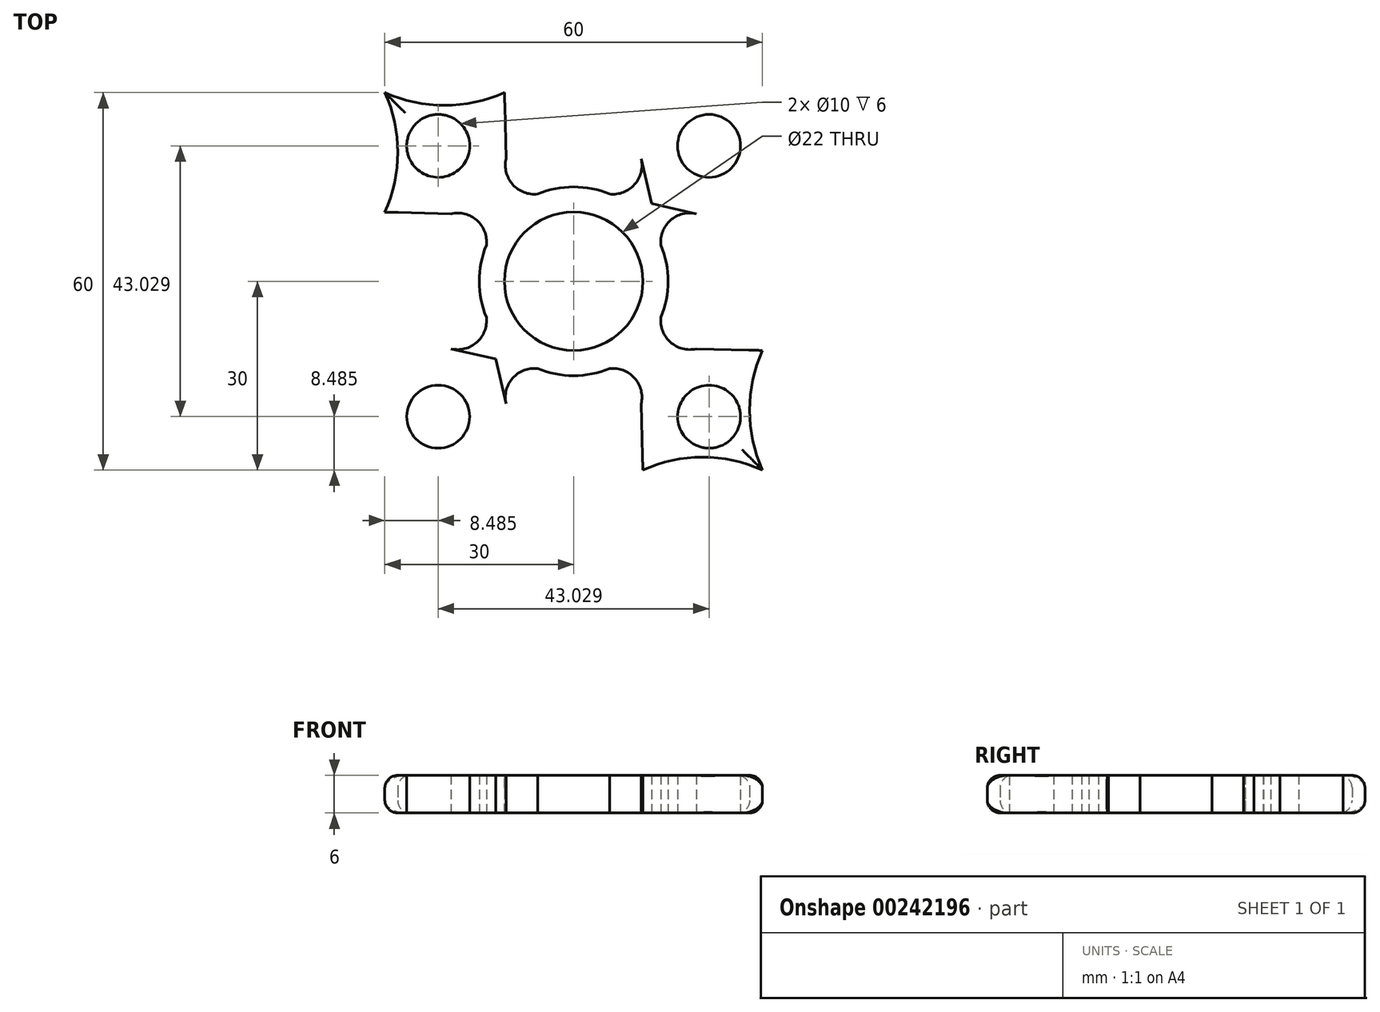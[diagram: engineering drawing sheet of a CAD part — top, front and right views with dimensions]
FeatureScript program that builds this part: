
annotation { "Feature Type Name" : "Feature", "Feature Type Description" : "" }
export const myFeature = defineFeature(function(context is Context, id is Id, definition is map)
    precondition{}
    {
        {
            var Q0;
            Q0=qCreatedBy(makeId("Top.planeOp"),FACE);
            var sketch = newSketch(context, id + "F0", { "sketchPlane" : qUnion([Q0])});
            skLineSegment(sketch, "E0.bottom", {"start": v(30, -30) * mm, "end": v(-30, -30) * mm});
            skLineSegment(sketch, "E0.top", {"start": v(30, 30) * mm, "end": v(-30, 30) * mm});
            skLineSegment(sketch, "E0.left", {"start": v(30, -30) * mm, "end": v(30, 30) * mm});
            skLineSegment(sketch, "E0.right", {"start": v(-30, -30) * mm, "end": v(-30, 30) * mm});
            skPoint(sketch, "E0.middle", {"position": v(0, 0) * mm});
            skCircle(sketch, "E1", {"center": v(0, 0) * mm, "radius": 11 * mm});
            skLineSegment(sketch, "E2", {"start": v(-30, 30) * mm, "end": v(30, -30) * mm, "construction": true});
            skCircle(sketch, "E3", {"center": v(-21.51, 21.51) * mm, "radius": 5 * mm});
            skCircle(sketch, "E4.MirrorC", {"center": v(21.51, 21.51) * mm, "radius": 5 * mm});
            skCircle(sketch, "E5.MirrorC", {"center": v(-21.51, -21.51) * mm, "radius": 5 * mm});
            skCircle(sketch, "E6.MirrorC", {"center": v(21.51, -21.51) * mm, "radius": 5 * mm});
            skCircle(sketch, "E7", {"center": v(0, 0) * mm, "radius": 15 * mm});
            skLineSegment(sketch, "E8", {"start": v(-10.99, 30) * mm, "end": v(-10.53, 10.68) * mm});
            skLineSegment(sketch, "E9.MirrorCS", {"start": v(10.99, 30) * mm, "end": v(10.53, 10.68) * mm});
            skLineSegment(sketch, "E10.MirrorCS", {"start": v(-10.99, -30) * mm, "end": v(-10.53, -10.68) * mm});
            skLineSegment(sketch, "E11.MirrorCS", {"start": v(10.99, -30) * mm, "end": v(10.53, -10.68) * mm});
            skLineSegment(sketch, "E12.MirrorCS", {"start": v(-30, 10.99) * mm, "end": v(-10.68, 10.53) * mm});
            skLineSegment(sketch, "E13.MirrorCS", {"start": v(-30, -10.99) * mm, "end": v(-10.68, -10.53) * mm});
            skLineSegment(sketch, "E14.MirrorCS", {"start": v(30, 10.99) * mm, "end": v(10.68, 10.53) * mm});
            skLineSegment(sketch, "E15.MirrorCS", {"start": v(30, -10.99) * mm, "end": v(10.68, -10.53) * mm});
            skLineSegment(sketch, "E16", {"start": v(30, -30) * mm, "end": v(-49.77, 49.77) * mm, "construction": true});
            skLineSegment(sketch, "E17", {"start": v(-5.73, -13.86) * mm, "end": v(-19.48, -10.74) * mm});
            skLineSegment(sketch, "E18.MirrorCS", {"start": v(5.73, -13.86) * mm, "end": v(19.48, -10.74) * mm});
            skLineSegment(sketch, "E19.MirrorCS", {"start": v(13.86, 5.73) * mm, "end": v(10.74, 19.48) * mm});
            skLineSegment(sketch, "E20.MirrorCS", {"start": v(13.86, -5.73) * mm, "end": v(10.74, -19.48) * mm});
            skLineSegment(sketch, "E21.MirrorCS", {"start": v(-13.86, 5.73) * mm, "end": v(-10.74, 19.48) * mm});
            skLineSegment(sketch, "E22.MirrorCS", {"start": v(-13.86, -5.73) * mm, "end": v(-10.74, -19.48) * mm});
            skLineSegment(sketch, "E23.MirrorCS", {"start": v(-5.73, 13.86) * mm, "end": v(-19.48, 10.74) * mm});
            skLineSegment(sketch, "E24.MirrorCS", {"start": v(5.73, 13.86) * mm, "end": v(19.48, 10.74) * mm});
            skArc(sketch, "E25", {"start": v(-30, 30) * mm, "mid": v(-20.5, 27.96) * mm, "end": v(-10.99, 30) * mm});
            skArc(sketch, "E26.MirrorCS", {"start": v(-30, -30) * mm, "mid": v(-20.5, -27.96) * mm, "end": v(-10.99, -30) * mm});
            skArc(sketch, "E27.MirrorCS", {"start": v(-30, 30) * mm, "mid": v(-27.96, 20.5) * mm, "end": v(-30, 10.99) * mm});
            skArc(sketch, "E28.MirrorCS", {"start": v(-30, -30) * mm, "mid": v(-27.96, -20.5) * mm, "end": v(-30, -10.99) * mm});
            skArc(sketch, "E29.MirrorCS", {"start": v(30, 30) * mm, "mid": v(20.5, 27.96) * mm, "end": v(10.99, 30) * mm});
            skArc(sketch, "E30.MirrorCS", {"start": v(30, 30) * mm, "mid": v(27.96, 20.5) * mm, "end": v(30, 10.99) * mm});
            skArc(sketch, "E31.MirrorCS", {"start": v(30, -30) * mm, "mid": v(27.96, -20.5) * mm, "end": v(30, -10.99) * mm});
            skArc(sketch, "E32.MirrorCS", {"start": v(30, -30) * mm, "mid": v(20.5, -27.96) * mm, "end": v(10.99, -30) * mm});
            skArc(sketch, "E33", {"start": v(-10.74, 19.48) * mm, "mid": v(-9.68, 15.38) * mm, "end": v(-5.73, 13.86) * mm});
            skArc(sketch, "E34.MirrorCS", {"start": v(-19.48, 10.74) * mm, "mid": v(-15.38, 9.68) * mm, "end": v(-13.86, 5.73) * mm});
            skArc(sketch, "E35.MirrorCS", {"start": v(10.74, 19.48) * mm, "mid": v(9.68, 15.38) * mm, "end": v(5.73, 13.86) * mm});
            skArc(sketch, "E36.MirrorCS", {"start": v(19.48, 10.74) * mm, "mid": v(15.38, 9.68) * mm, "end": v(13.86, 5.73) * mm});
            skArc(sketch, "E37.MirrorCS", {"start": v(-19.48, -10.74) * mm, "mid": v(-15.38, -9.68) * mm, "end": v(-13.86, -5.73) * mm});
            skArc(sketch, "E38.MirrorCS", {"start": v(-10.74, -19.48) * mm, "mid": v(-9.68, -15.38) * mm, "end": v(-5.73, -13.86) * mm});
            skArc(sketch, "E39.MirrorCS", {"start": v(10.74, -19.48) * mm, "mid": v(9.68, -15.38) * mm, "end": v(5.73, -13.86) * mm});
            skArc(sketch, "E40.MirrorCS", {"start": v(19.48, -10.74) * mm, "mid": v(15.38, -9.68) * mm, "end": v(13.86, -5.73) * mm});
            skSolve(sketch);
        }
        {
            var Q0;
            Q0=makeQuery(id+"F0.imprint","IMPRINT",FACE,{"disambiguationData":[TD([[makeQuery(id+"F0.imprint","IMPRINT",EDGE,{"derivedFrom":sQuery(id+"F0.wireOp",EDGE,"E1")}),-1.0]])]});
            var Q1;
            {var subQ5=sQuery(id+"F0.wireOp",EDGE,"Vc4GJ9Qz-F7U4-Q4aa-D5jw-WVhD1GYveR6j");var subQ6=sQuery(id+"F0.wireOp",EDGE,"E3");var subQ7=makeQuery(id+"F0.imprint","INTERSECT",VERTEX,{"disambiguationData":[OD(0.0)],"derivedFrom":[subQ6,subQ5]});Q1=makeQuery(id+"F0.imprint","IMPRINT",FACE,{"disambiguationData":[TD([[makeQuery(id+"F0.imprint","IMPRINT",EDGE,{"disambiguationData":[TD([[subQ7,-1.0]])],"derivedFrom":subQ6}),-1.0]])]});}
            var Q2;
            {var subQ1=sQuery(id+"F0.wireOp",EDGE,"E0.top");var subQ3=sQuery(id+"F0.wireOp",EDGE,"gGmC0kKu-PqWo-ojIo-RihK-eTT0kTxVYyVW");var subQ4=makeQuery(id+"F0.imprint","INTERSECT",VERTEX,{"disambiguationData":[OD(0.0)],"derivedFrom":[subQ1,subQ3]});Q2=makeQuery(id+"F0.imprint","IMPRINT",FACE,{"disambiguationData":[TD([[makeQuery(id+"F0.imprint","IMPRINT",EDGE,{"disambiguationData":[TD([[subQ4,-1.0]])],"derivedFrom":subQ3}),1.0]])]});}
            var Q3;
            {var subQ5=sQuery(id+"F0.wireOp",EDGE,"Vc4GJ9Qz-F7U4-Q4aa-D5jw-WVhD1GYveR6j");var subQ6=sQuery(id+"F0.wireOp",EDGE,"E4.MirrorC");var subQ7=makeQuery(id+"F0.imprint","INTERSECT",VERTEX,{"disambiguationData":[OD(0.0)],"derivedFrom":[subQ6,subQ5]});Q3=makeQuery(id+"F0.imprint","IMPRINT",FACE,{"disambiguationData":[TD([[makeQuery(id+"F0.imprint","IMPRINT",EDGE,{"disambiguationData":[TD([[subQ7,1.0]])],"derivedFrom":subQ6}),1.0]])]});}
            var Q4;
            {var subQ1=sQuery(id+"F0.wireOp",EDGE,"E0.left");var subQ3=sQuery(id+"F0.wireOp",EDGE,"gGmC0kKu-PqWo-ojIo-RihK-eTT0kTxVYyVW");var subQ4=makeQuery(id+"F0.imprint","INTERSECT",VERTEX,{"disambiguationData":[OD(0.0)],"derivedFrom":[subQ1,subQ3]});Q4=makeQuery(id+"F0.imprint","IMPRINT",FACE,{"disambiguationData":[TD([[makeQuery(id+"F0.imprint","IMPRINT",EDGE,{"disambiguationData":[TD([[subQ4,-1.0]])],"derivedFrom":subQ3}),1.0]])]});}
            var Q5;
            {var subQ5=sQuery(id+"F0.wireOp",EDGE,"Vc4GJ9Qz-F7U4-Q4aa-D5jw-WVhD1GYveR6j");var subQ6=sQuery(id+"F0.wireOp",EDGE,"E6.MirrorC");var subQ7=makeQuery(id+"F0.imprint","INTERSECT",VERTEX,{"disambiguationData":[OD(0.0)],"derivedFrom":[subQ6,subQ5]});Q5=makeQuery(id+"F0.imprint","IMPRINT",FACE,{"disambiguationData":[TD([[makeQuery(id+"F0.imprint","IMPRINT",EDGE,{"disambiguationData":[TD([[subQ7,-1.0]])],"derivedFrom":subQ6}),-1.0]])]});}
            var Q6;
            {var subQ1=sQuery(id+"F0.wireOp",EDGE,"E0.bottom");var subQ3=sQuery(id+"F0.wireOp",EDGE,"gGmC0kKu-PqWo-ojIo-RihK-eTT0kTxVYyVW");var subQ4=makeQuery(id+"F0.imprint","INTERSECT",VERTEX,{"disambiguationData":[OD(0.0)],"derivedFrom":[subQ1,subQ3]});Q6=makeQuery(id+"F0.imprint","IMPRINT",FACE,{"disambiguationData":[TD([[makeQuery(id+"F0.imprint","IMPRINT",EDGE,{"disambiguationData":[TD([[subQ4,1.0]])],"derivedFrom":subQ3}),1.0]])]});}
            var Q7;
            {var subQ0=sQuery(id+"F0.wireOp",EDGE,"Vc4GJ9Qz-F7U4-Q4aa-D5jw-WVhD1GYveR6j");var subQ1=sQuery(id+"F0.wireOp",EDGE,"E5.MirrorC");var subQ2=makeQuery(id+"F0.imprint","INTERSECT",VERTEX,{"disambiguationData":[OD(0.0)],"derivedFrom":[subQ1,subQ0]});Q7=makeQuery(id+"F0.imprint","IMPRINT",FACE,{"disambiguationData":[TD([[makeQuery(id+"F0.imprint","IMPRINT",EDGE,{"disambiguationData":[TD([[subQ2,1.0]])],"derivedFrom":subQ1}),1.0]])]});}
            var Q8;
            {var subQ1=sQuery(id+"F0.wireOp",EDGE,"E0.right");var subQ3=sQuery(id+"F0.wireOp",EDGE,"gGmC0kKu-PqWo-ojIo-RihK-eTT0kTxVYyVW");var subQ4=makeQuery(id+"F0.imprint","INTERSECT",VERTEX,{"disambiguationData":[OD(0.0)],"derivedFrom":[subQ1,subQ3]});Q8=makeQuery(id+"F0.imprint","IMPRINT",FACE,{"disambiguationData":[TD([[makeQuery(id+"F0.imprint","IMPRINT",EDGE,{"disambiguationData":[TD([[subQ4,1.0]])],"derivedFrom":subQ3}),1.0]])]});}
            var Q9;
            {var subQ0=sQuery(id+"F0.wireOp",EDGE,"E0.right");var subQ1=sQuery(id+"F0.wireOp",EDGE,"E0.top");var subQ2=makeQuery(id+"F0.imprint","INTERSECT",VERTEX,{"derivedFrom":[subQ1,subQ0]});Q9=makeQuery(id+"F0.imprint","IMPRINT",FACE,{"disambiguationData":[TD([[makeQuery(id+"F0.imprint","IMPRINT",EDGE,{"disambiguationData":[TD([[subQ2,1.0]])],"derivedFrom":subQ1}),-1.0]])]});}
            var Q10;
            {var subQ0=sQuery(id+"F0.wireOp",EDGE,"E0.right");var subQ1=sQuery(id+"F0.wireOp",EDGE,"E0.bottom");var subQ2=makeQuery(id+"F0.imprint","INTERSECT",VERTEX,{"derivedFrom":[subQ1,subQ0]});Q10=makeQuery(id+"F0.imprint","IMPRINT",FACE,{"disambiguationData":[TD([[makeQuery(id+"F0.imprint","IMPRINT",EDGE,{"disambiguationData":[TD([[subQ2,1.0]])],"derivedFrom":subQ1}),1.0]])]});}
            var Q11;
            {var subQ0=sQuery(id+"F0.wireOp",EDGE,"E0.left");var subQ1=sQuery(id+"F0.wireOp",EDGE,"E0.bottom");var subQ2=makeQuery(id+"F0.imprint","INTERSECT",VERTEX,{"derivedFrom":[subQ1,subQ0]});Q11=makeQuery(id+"F0.imprint","IMPRINT",FACE,{"disambiguationData":[TD([[makeQuery(id+"F0.imprint","IMPRINT",EDGE,{"disambiguationData":[TD([[subQ2,-1.0]])],"derivedFrom":subQ1}),1.0]])]});}
            var Q12;
            {var subQ0=sQuery(id+"F0.wireOp",EDGE,"E0.left");var subQ1=sQuery(id+"F0.wireOp",EDGE,"E0.top");var subQ2=makeQuery(id+"F0.imprint","INTERSECT",VERTEX,{"derivedFrom":[subQ1,subQ0]});Q12=makeQuery(id+"F0.imprint","IMPRINT",FACE,{"disambiguationData":[TD([[makeQuery(id+"F0.imprint","IMPRINT",EDGE,{"disambiguationData":[TD([[subQ2,-1.0]])],"derivedFrom":subQ1}),-1.0]])]});}
            var Q13;
            {var subQ3=sQuery(id+"F0.wireOp",EDGE,"E23.MirrorCS");Q13=makeQuery(id+"F0.imprint","IMPRINT",FACE,{"disambiguationData":[TD([[makeQuery(id+"F0.imprint","IMPRINT",EDGE,{"derivedFrom":subQ3}),-1.0]])]});}
            var Q14;
            {var subQ3=sQuery(id+"F0.wireOp",EDGE,"E17");Q14=makeQuery(id+"F0.imprint","IMPRINT",FACE,{"disambiguationData":[TD([[makeQuery(id+"F0.imprint","IMPRINT",EDGE,{"derivedFrom":subQ3}),1.0]])]});}
            var Q15;
            {var subQ3=sQuery(id+"F0.wireOp",EDGE,"E22.MirrorCS");Q15=makeQuery(id+"F0.imprint","IMPRINT",FACE,{"disambiguationData":[TD([[makeQuery(id+"F0.imprint","IMPRINT",EDGE,{"derivedFrom":subQ3}),-1.0]])]});}
            var Q16;
            {var subQ3=sQuery(id+"F0.wireOp",EDGE,"E20.MirrorCS");Q16=makeQuery(id+"F0.imprint","IMPRINT",FACE,{"disambiguationData":[TD([[makeQuery(id+"F0.imprint","IMPRINT",EDGE,{"derivedFrom":subQ3}),1.0]])]});}
            var Q17;
            {var subQ3=sQuery(id+"F0.wireOp",EDGE,"E18.MirrorCS");Q17=makeQuery(id+"F0.imprint","IMPRINT",FACE,{"disambiguationData":[TD([[makeQuery(id+"F0.imprint","IMPRINT",EDGE,{"derivedFrom":subQ3}),-1.0]])]});}
            var Q18;
            {var subQ3=sQuery(id+"F0.wireOp",EDGE,"E24.MirrorCS");Q18=makeQuery(id+"F0.imprint","IMPRINT",FACE,{"disambiguationData":[TD([[makeQuery(id+"F0.imprint","IMPRINT",EDGE,{"derivedFrom":subQ3}),1.0]])]});}
            var Q19;
            {var subQ3=sQuery(id+"F0.wireOp",EDGE,"E19.MirrorCS");Q19=makeQuery(id+"F0.imprint","IMPRINT",FACE,{"disambiguationData":[TD([[makeQuery(id+"F0.imprint","IMPRINT",EDGE,{"derivedFrom":subQ3}),-1.0]])]});}
            var Q20;
            {var subQ3=sQuery(id+"F0.wireOp",EDGE,"E21.MirrorCS");Q20=makeQuery(id+"F0.imprint","IMPRINT",FACE,{"disambiguationData":[TD([[makeQuery(id+"F0.imprint","IMPRINT",EDGE,{"derivedFrom":subQ3}),1.0]])]});}
            var Q21;
            {var subQ0=sQuery(id+"F0.wireOp",EDGE,"E12.MirrorCS");var subQ1=sQuery(id+"F0.wireOp",EDGE,"E7");var subQ2=makeQuery(id+"F0.imprint","INTERSECT",VERTEX,{"derivedFrom":[subQ1,subQ0]});Q21=makeQuery(id+"F0.imprint","IMPRINT",FACE,{"disambiguationData":[TD([[makeQuery(id+"F0.imprint","IMPRINT",EDGE,{"disambiguationData":[TD([[subQ2,-1.0]])],"derivedFrom":subQ1}),-1.0]])]});}
            var Q22;
            {var subQ0=sQuery(id+"F0.wireOp",EDGE,"E8");var subQ1=sQuery(id+"F0.wireOp",EDGE,"E7");var subQ2=makeQuery(id+"F0.imprint","INTERSECT",VERTEX,{"derivedFrom":[subQ1,subQ0]});Q22=makeQuery(id+"F0.imprint","IMPRINT",FACE,{"disambiguationData":[TD([[makeQuery(id+"F0.imprint","IMPRINT",EDGE,{"disambiguationData":[TD([[subQ2,1.0]])],"derivedFrom":subQ1}),-1.0]])]});}
            var Q23;
            {var subQ5=sQuery(id+"F0.wireOp",EDGE,"E7");var subQ7=sQuery(id+"F0.wireOp",EDGE,"E9.MirrorCS");var subQ8=makeQuery(id+"F0.imprint","INTERSECT",VERTEX,{"derivedFrom":[subQ5,subQ7]});Q23=makeQuery(id+"F0.imprint","IMPRINT",FACE,{"disambiguationData":[TD([[makeQuery(id+"F0.imprint","IMPRINT",EDGE,{"disambiguationData":[TD([[subQ8,1.0]])],"derivedFrom":subQ5}),-1.0]])]});}
            var Q24;
            {var subQ0=sQuery(id+"F0.wireOp",EDGE,"E9.MirrorCS");var subQ1=sQuery(id+"F0.wireOp",EDGE,"E7");var subQ2=makeQuery(id+"F0.imprint","INTERSECT",VERTEX,{"derivedFrom":[subQ1,subQ0]});Q24=makeQuery(id+"F0.imprint","IMPRINT",FACE,{"disambiguationData":[TD([[makeQuery(id+"F0.imprint","IMPRINT",EDGE,{"disambiguationData":[TD([[subQ2,-1.0]])],"derivedFrom":subQ1}),-1.0]])]});}
            var Q25;
            {var subQ0=sQuery(id+"F0.wireOp",EDGE,"E14.MirrorCS");var subQ1=sQuery(id+"F0.wireOp",EDGE,"E7");var subQ2=makeQuery(id+"F0.imprint","INTERSECT",VERTEX,{"derivedFrom":[subQ1,subQ0]});Q25=makeQuery(id+"F0.imprint","IMPRINT",FACE,{"disambiguationData":[TD([[makeQuery(id+"F0.imprint","IMPRINT",EDGE,{"disambiguationData":[TD([[subQ2,1.0]])],"derivedFrom":subQ1}),-1.0]])]});}
            var Q26;
            {var subQ5=sQuery(id+"F0.wireOp",EDGE,"E7");var subQ7=sQuery(id+"F0.wireOp",EDGE,"E8");var subQ8=makeQuery(id+"F0.imprint","INTERSECT",VERTEX,{"derivedFrom":[subQ5,subQ7]});Q26=makeQuery(id+"F0.imprint","IMPRINT",FACE,{"disambiguationData":[TD([[makeQuery(id+"F0.imprint","IMPRINT",EDGE,{"disambiguationData":[TD([[subQ8,-1.0]])],"derivedFrom":subQ5}),-1.0]])]});}
            var Q27;
            {var subQ1=sQuery(id+"F0.wireOp",EDGE,"E7");var subQ6=sQuery(id+"F0.wireOp",EDGE,"E10.MirrorCS");var subQ9=makeQuery(id+"F0.imprint","INTERSECT",VERTEX,{"derivedFrom":[subQ1,subQ6]});Q27=makeQuery(id+"F0.imprint","IMPRINT",FACE,{"disambiguationData":[TD([[makeQuery(id+"F0.imprint","IMPRINT",EDGE,{"disambiguationData":[TD([[subQ9,1.0]])],"derivedFrom":subQ1}),-1.0]])]});}
            var Q28;
            {var subQ1=sQuery(id+"F0.wireOp",EDGE,"E7");var subQ6=sQuery(id+"F0.wireOp",EDGE,"E11.MirrorCS");var subQ9=makeQuery(id+"F0.imprint","INTERSECT",VERTEX,{"derivedFrom":[subQ1,subQ6]});Q28=makeQuery(id+"F0.imprint","IMPRINT",FACE,{"disambiguationData":[TD([[makeQuery(id+"F0.imprint","IMPRINT",EDGE,{"disambiguationData":[TD([[subQ9,-1.0]])],"derivedFrom":subQ1}),-1.0]])]});}
            var Q29;
            {var subQ0=sQuery(id+"F0.wireOp",EDGE,"E13.MirrorCS");var subQ1=sQuery(id+"F0.wireOp",EDGE,"E7");var subQ2=makeQuery(id+"F0.imprint","INTERSECT",VERTEX,{"derivedFrom":[subQ1,subQ0]});Q29=makeQuery(id+"F0.imprint","IMPRINT",FACE,{"disambiguationData":[TD([[makeQuery(id+"F0.imprint","IMPRINT",EDGE,{"disambiguationData":[TD([[subQ2,1.0]])],"derivedFrom":subQ1}),-1.0]])]});}
            var Q30;
            {var subQ0=sQuery(id+"F0.wireOp",EDGE,"E10.MirrorCS");var subQ1=sQuery(id+"F0.wireOp",EDGE,"E7");var subQ2=makeQuery(id+"F0.imprint","INTERSECT",VERTEX,{"derivedFrom":[subQ1,subQ0]});Q30=makeQuery(id+"F0.imprint","IMPRINT",FACE,{"disambiguationData":[TD([[makeQuery(id+"F0.imprint","IMPRINT",EDGE,{"disambiguationData":[TD([[subQ2,-1.0]])],"derivedFrom":subQ1}),-1.0]])]});}
            var Q31;
            {var subQ0=sQuery(id+"F0.wireOp",EDGE,"E11.MirrorCS");var subQ1=sQuery(id+"F0.wireOp",EDGE,"E7");var subQ2=makeQuery(id+"F0.imprint","INTERSECT",VERTEX,{"derivedFrom":[subQ1,subQ0]});Q31=makeQuery(id+"F0.imprint","IMPRINT",FACE,{"disambiguationData":[TD([[makeQuery(id+"F0.imprint","IMPRINT",EDGE,{"disambiguationData":[TD([[subQ2,1.0]])],"derivedFrom":subQ1}),-1.0]])]});}
            var Q32;
            {var subQ0=sQuery(id+"F0.wireOp",EDGE,"E15.MirrorCS");var subQ1=sQuery(id+"F0.wireOp",EDGE,"E7");var subQ2=makeQuery(id+"F0.imprint","INTERSECT",VERTEX,{"derivedFrom":[subQ1,subQ0]});Q32=makeQuery(id+"F0.imprint","IMPRINT",FACE,{"disambiguationData":[TD([[makeQuery(id+"F0.imprint","IMPRINT",EDGE,{"disambiguationData":[TD([[subQ2,-1.0]])],"derivedFrom":subQ1}),-1.0]])]});}
            var Q33;
            {var subQ0=sQuery(id+"F0.wireOp",EDGE,"E33");var subQ1=sQuery(id+"F0.wireOp",EDGE,"E8");var subQ2=makeQuery(id+"F0.imprint","INTERSECT",VERTEX,{"derivedFrom":[subQ1,subQ0]});Q33=makeQuery(id+"F0.imprint","IMPRINT",FACE,{"disambiguationData":[TD([[makeQuery(id+"F0.imprint","IMPRINT",EDGE,{"disambiguationData":[TD([[subQ2,-1.0]])],"derivedFrom":subQ1}),-1.0]])]});}
            var Q34;
            {var subQ0=sQuery(id+"F0.wireOp",EDGE,"E34.MirrorCS");var subQ1=sQuery(id+"F0.wireOp",EDGE,"E12.MirrorCS");var subQ2=makeQuery(id+"F0.imprint","INTERSECT",VERTEX,{"derivedFrom":[subQ1,subQ0]});Q34=makeQuery(id+"F0.imprint","IMPRINT",FACE,{"disambiguationData":[TD([[makeQuery(id+"F0.imprint","IMPRINT",EDGE,{"disambiguationData":[TD([[subQ2,-1.0]])],"derivedFrom":subQ1}),1.0]])]});}
            var Q35;
            {var subQ0=sQuery(id+"F0.wireOp",EDGE,"E37.MirrorCS");var subQ1=sQuery(id+"F0.wireOp",EDGE,"E13.MirrorCS");var subQ2=makeQuery(id+"F0.imprint","INTERSECT",VERTEX,{"derivedFrom":[subQ1,subQ0]});Q35=makeQuery(id+"F0.imprint","IMPRINT",FACE,{"disambiguationData":[TD([[makeQuery(id+"F0.imprint","IMPRINT",EDGE,{"disambiguationData":[TD([[subQ2,-1.0]])],"derivedFrom":subQ1}),-1.0]])]});}
            var Q36;
            {var subQ0=sQuery(id+"F0.wireOp",EDGE,"E38.MirrorCS");var subQ1=sQuery(id+"F0.wireOp",EDGE,"E10.MirrorCS");var subQ2=makeQuery(id+"F0.imprint","INTERSECT",VERTEX,{"derivedFrom":[subQ1,subQ0]});Q36=makeQuery(id+"F0.imprint","IMPRINT",FACE,{"disambiguationData":[TD([[makeQuery(id+"F0.imprint","IMPRINT",EDGE,{"disambiguationData":[TD([[subQ2,-1.0]])],"derivedFrom":subQ1}),1.0]])]});}
            var Q37;
            {var subQ0=sQuery(id+"F0.wireOp",EDGE,"E39.MirrorCS");var subQ1=sQuery(id+"F0.wireOp",EDGE,"E11.MirrorCS");var subQ2=makeQuery(id+"F0.imprint","INTERSECT",VERTEX,{"derivedFrom":[subQ1,subQ0]});Q37=makeQuery(id+"F0.imprint","IMPRINT",FACE,{"disambiguationData":[TD([[makeQuery(id+"F0.imprint","IMPRINT",EDGE,{"disambiguationData":[TD([[subQ2,-1.0]])],"derivedFrom":subQ1}),-1.0]])]});}
            var Q38;
            {var subQ0=sQuery(id+"F0.wireOp",EDGE,"E40.MirrorCS");var subQ1=sQuery(id+"F0.wireOp",EDGE,"E15.MirrorCS");var subQ2=makeQuery(id+"F0.imprint","INTERSECT",VERTEX,{"derivedFrom":[subQ1,subQ0]});Q38=makeQuery(id+"F0.imprint","IMPRINT",FACE,{"disambiguationData":[TD([[makeQuery(id+"F0.imprint","IMPRINT",EDGE,{"disambiguationData":[TD([[subQ2,-1.0]])],"derivedFrom":subQ1}),1.0]])]});}
            var Q39;
            {var subQ0=sQuery(id+"F0.wireOp",EDGE,"E36.MirrorCS");var subQ1=sQuery(id+"F0.wireOp",EDGE,"E14.MirrorCS");var subQ2=makeQuery(id+"F0.imprint","INTERSECT",VERTEX,{"derivedFrom":[subQ1,subQ0]});Q39=makeQuery(id+"F0.imprint","IMPRINT",FACE,{"disambiguationData":[TD([[makeQuery(id+"F0.imprint","IMPRINT",EDGE,{"disambiguationData":[TD([[subQ2,-1.0]])],"derivedFrom":subQ1}),-1.0]])]});}
            var Q40;
            {var subQ0=sQuery(id+"F0.wireOp",EDGE,"E35.MirrorCS");var subQ1=sQuery(id+"F0.wireOp",EDGE,"E9.MirrorCS");var subQ2=makeQuery(id+"F0.imprint","INTERSECT",VERTEX,{"derivedFrom":[subQ1,subQ0]});Q40=makeQuery(id+"F0.imprint","IMPRINT",FACE,{"disambiguationData":[TD([[makeQuery(id+"F0.imprint","IMPRINT",EDGE,{"disambiguationData":[TD([[subQ2,-1.0]])],"derivedFrom":subQ1}),1.0]])]});}
            extrude(context, id + "F1", {"entities" : qUnion([Q0, Q1, Q2, Q3, Q4, Q5, Q6, Q7, Q8, Q9, Q10, Q11, Q12, Q13, Q14, Q15, Q16, Q17, Q18, Q19, Q20, Q21, Q22, Q23, Q24, Q25, Q26, Q27, Q28, Q29, Q30, Q31, Q32, Q33, Q34, Q35, Q36, Q37, Q38, Q39, Q40]), "depth" : 6 * mm, "offsetDistance" : 25 * mm});
        }
        {
            var Q0;
            Q0=makeQuery(id+"F1.opExtrude","CAP_EDGE",EDGE,{"disambiguationData":[OSD([sQuery(id+"F0.wireOp",EDGE,"E25")])],"isStart":false});
            var Q1;
            Q1=makeQuery(id+"F1.opExtrude","CAP_EDGE",EDGE,{"disambiguationData":[OSD([sQuery(id+"F0.wireOp",EDGE,"E27.MirrorCS")])],"isStart":false});
            var Q2;
            Q2=makeQuery(id+"F1.opExtrude","CAP_EDGE",EDGE,{"disambiguationData":[OSD([sQuery(id+"F0.wireOp",EDGE,"E25")])],"isStart":true});
            var Q3;
            Q3=makeQuery(id+"F1.opExtrude","CAP_EDGE",EDGE,{"disambiguationData":[OSD([sQuery(id+"F0.wireOp",EDGE,"E27.MirrorCS")])],"isStart":true});
            var Q4;
            Q4=makeQuery(id+"F1.opExtrude","CAP_EDGE",EDGE,{"disambiguationData":[OSD([sQuery(id+"F0.wireOp",EDGE,"E29.MirrorCS")])],"isStart":false});
            var Q5;
            Q5=makeQuery(id+"F1.opExtrude","CAP_EDGE",EDGE,{"disambiguationData":[OSD([sQuery(id+"F0.wireOp",EDGE,"E29.MirrorCS")])],"isStart":true});
            var Q6;
            Q6=makeQuery(id+"F1.opExtrude","CAP_EDGE",EDGE,{"disambiguationData":[OSD([sQuery(id+"F0.wireOp",EDGE,"E30.MirrorCS")])],"isStart":false});
            var Q7;
            Q7=makeQuery(id+"F1.opExtrude","CAP_EDGE",EDGE,{"disambiguationData":[OSD([sQuery(id+"F0.wireOp",EDGE,"E28.MirrorCS")])],"isStart":false});
            var Q8;
            Q8=makeQuery(id+"F1.opExtrude","CAP_EDGE",EDGE,{"disambiguationData":[OSD([sQuery(id+"F0.wireOp",EDGE,"E31.MirrorCS")])],"isStart":false});
            var Q9;
            Q9=makeQuery(id+"F1.opExtrude","CAP_EDGE",EDGE,{"disambiguationData":[OSD([sQuery(id+"F0.wireOp",EDGE,"E32.MirrorCS")])],"isStart":false});
            var Q10;
            Q10=makeQuery(id+"F1.opExtrude","CAP_EDGE",EDGE,{"disambiguationData":[OSD([sQuery(id+"F0.wireOp",EDGE,"E26.MirrorCS")])],"isStart":false});
            var Q11;
            Q11=makeQuery(id+"F1.opExtrude","CAP_EDGE",EDGE,{"disambiguationData":[OSD([sQuery(id+"F0.wireOp",EDGE,"E31.MirrorCS")])],"isStart":true});
            var Q12;
            Q12=makeQuery(id+"F1.opExtrude","CAP_EDGE",EDGE,{"disambiguationData":[OSD([sQuery(id+"F0.wireOp",EDGE,"E30.MirrorCS")])],"isStart":true});
            var Q13;
            Q13=makeQuery(id+"F1.opExtrude","CAP_EDGE",EDGE,{"disambiguationData":[OSD([sQuery(id+"F0.wireOp",EDGE,"E32.MirrorCS")])],"isStart":true});
            var Q14;
            Q14=makeQuery(id+"F1.opExtrude","CAP_EDGE",EDGE,{"disambiguationData":[OSD([sQuery(id+"F0.wireOp",EDGE,"E26.MirrorCS")])],"isStart":true});
            var Q15;
            Q15=makeQuery(id+"F1.opExtrude","CAP_EDGE",EDGE,{"disambiguationData":[OSD([sQuery(id+"F0.wireOp",EDGE,"E28.MirrorCS")])],"isStart":true});
            fillet(context, id + "F2", {"entities" : qUnion([Q0, Q1, Q2, Q3, Q4, Q5, Q6, Q7, Q8, Q9, Q10, Q11, Q12, Q13, Q14, Q15]), "radius" : 2 * mm, "tangentPropagation" : true, "allowEdgeOverflow" : false});
        }
    });
